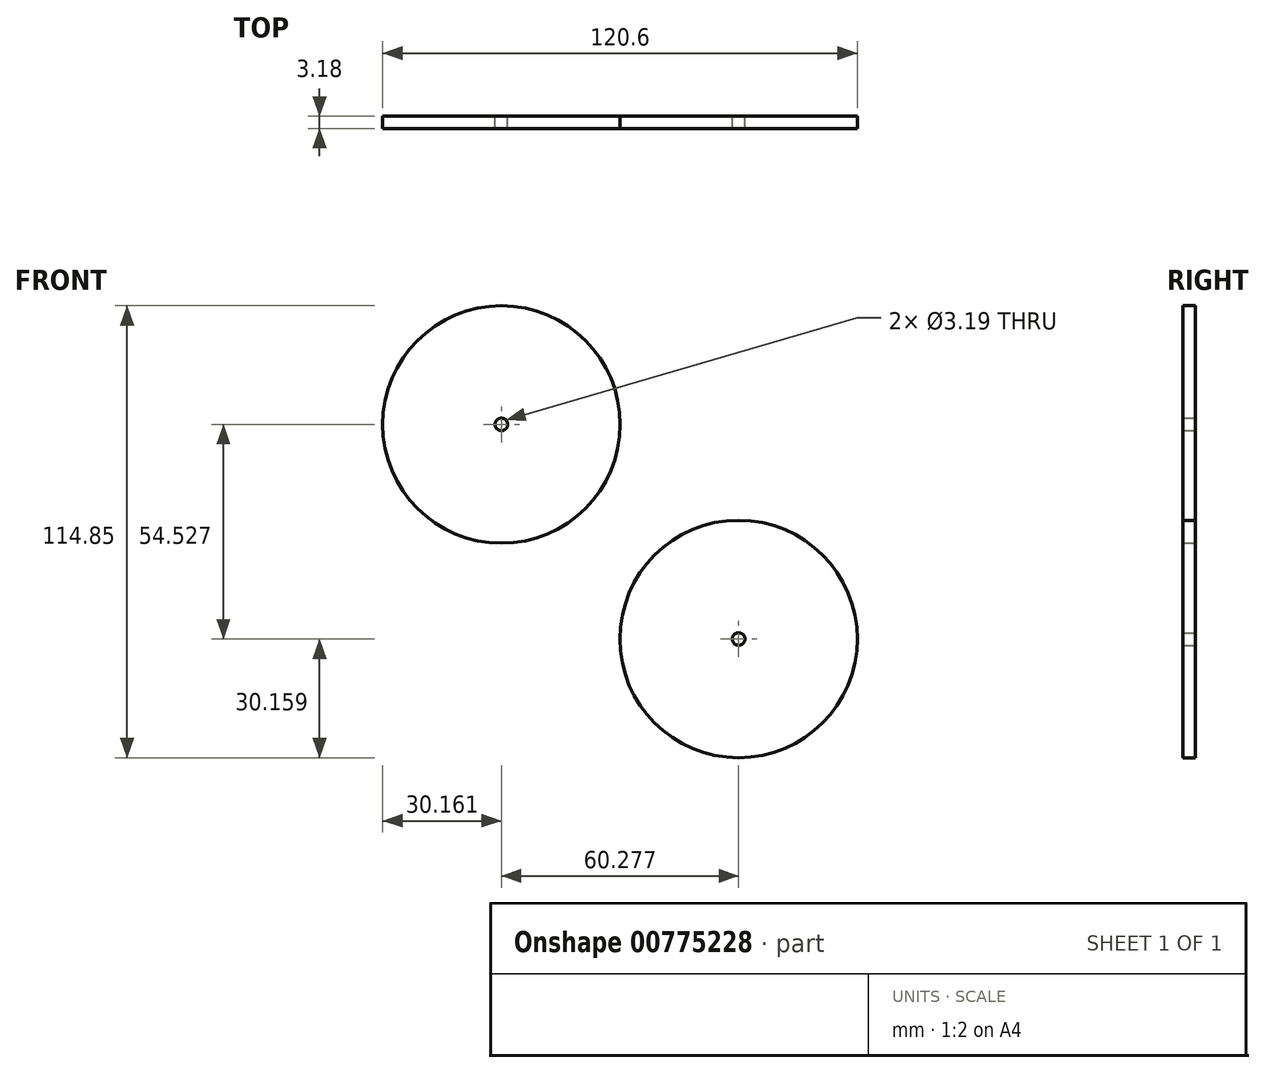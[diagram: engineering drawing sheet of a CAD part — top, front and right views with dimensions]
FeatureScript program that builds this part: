
annotation { "Feature Type Name" : "Feature", "Feature Type Description" : "" }
export const myFeature = defineFeature(function(context is Context, id is Id, definition is map)
    precondition{}
    {
        {
            var Q0;
            Q0=qCreatedBy(makeId("Front.planeOp"),FACE);
            var sketch = newSketch(context, id + "F0", { "sketchPlane" : qUnion([Q0])});
            skCircle(sketch, "E0", {"center": v(0, 0) * mm, "radius": 27.5 * mm});
            skCircle(sketch, "E1", {"center": v(0, 0) * mm, "radius": 1.64 * mm});
            skCircle(sketch, "E2", {"center": v(92.17, -25.39) * mm, "radius": 27.5 * mm});
            skCircle(sketch, "E3", {"center": v(92.17, -25.39) * mm, "radius": 1.64 * mm});
            skCircle(sketch, "E4", {"center": v(-93.5, -11.74) * mm, "radius": 30.16 * mm});
            skCircle(sketch, "E5", {"center": v(-93.5, -11.74) * mm, "radius": 1.6 * mm});
            skCircle(sketch, "E6", {"center": v(-33.23, -66.27) * mm, "radius": 30.16 * mm});
            skCircle(sketch, "E7", {"center": v(-33.23, -66.27) * mm, "radius": 1.6 * mm});
            skSolve(sketch);
        }
        {
            var Q0;
            Q0=makeQuery(id+"F0.imprint","IMPRINT",FACE,{"disambiguationData":[TD([[makeQuery(id+"F0.imprint","IMPRINT",EDGE,{"derivedFrom":sQuery(id+"F0.wireOp",EDGE,"E4")}),1.0]])]});
            extrude(context, id + "F1", {"entities" : qUnion([Q0]), "depth" : 3.17 * mm, "offsetDistance" : 25.4 * mm});
        }
        {
            var Q0;
            Q0=makeQuery(id+"F0.imprint","IMPRINT",FACE,{"disambiguationData":[TD([[makeQuery(id+"F0.imprint","IMPRINT",EDGE,{"derivedFrom":sQuery(id+"F0.wireOp",EDGE,"E6")}),1.0]])]});
            extrude(context, id + "F2", {"entities" : qUnion([Q0]), "depth" : 3.17 * mm, "offsetDistance" : 25.4 * mm});
        }
    });
